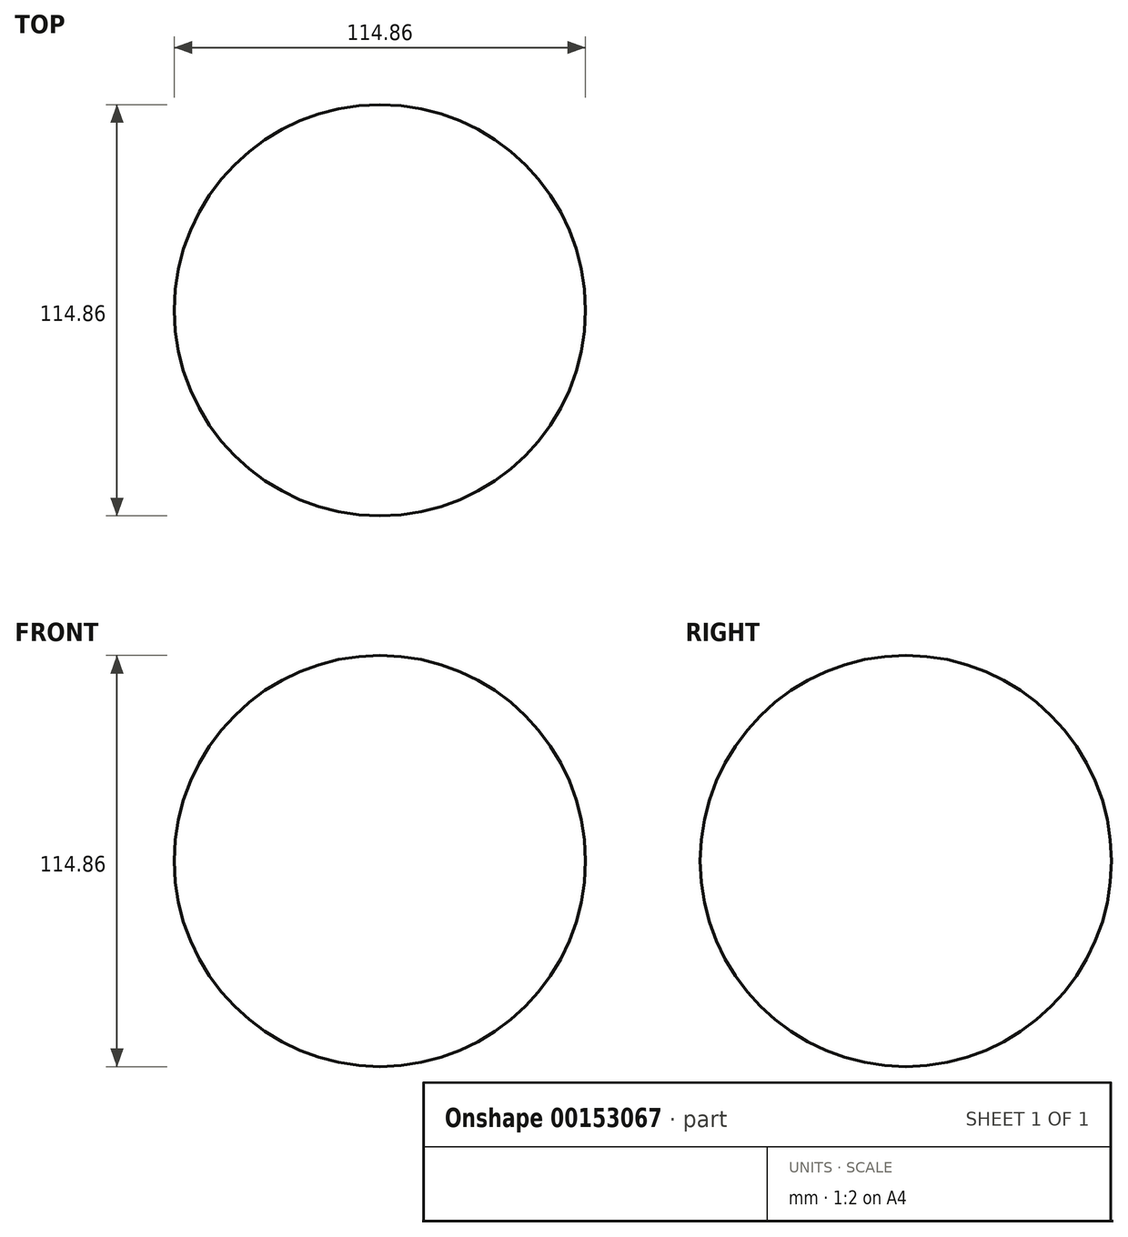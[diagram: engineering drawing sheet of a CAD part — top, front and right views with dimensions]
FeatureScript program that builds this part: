
annotation { "Feature Type Name" : "Feature", "Feature Type Description" : "" }
export const myFeature = defineFeature(function(context is Context, id is Id, definition is map)
    precondition{}
    {
        {
            var Q0;
            Q0=qCreatedBy(makeId("Top.planeOp"),FACE);
            var sketch = newSketch(context, id + "F0", { "sketchPlane" : qUnion([Q0])});
            skCircle(sketch, "E0", {"center": v(0, 0) * mm, "radius": 57.43 * mm});
            skLineSegment(sketch, "E1", {"start": v(0, -57.43) * mm, "end": v(0, 57.43) * mm});
            skSolve(sketch);
        }
        {
            var Q0;
            {var subQ0=sQuery(id+"F0.wireOp",EDGE,"E1");Q0=makeQuery(id+"F0.imprint","IMPRINT",FACE,{"disambiguationData":[TD([[makeQuery(id+"F0.imprint","IMPRINT",EDGE,{"derivedFrom":subQ0}),-1.0]])]});}
            var Q1;
            Q1=sQuery(id+"F0.wireOp",EDGE,"E1");
            revolve(context, id + "F1", {"entities" : qUnion([Q0]), "axis" : qUnion([Q1]), "revolveType" : RevolveType.FULL});
        }
    });
